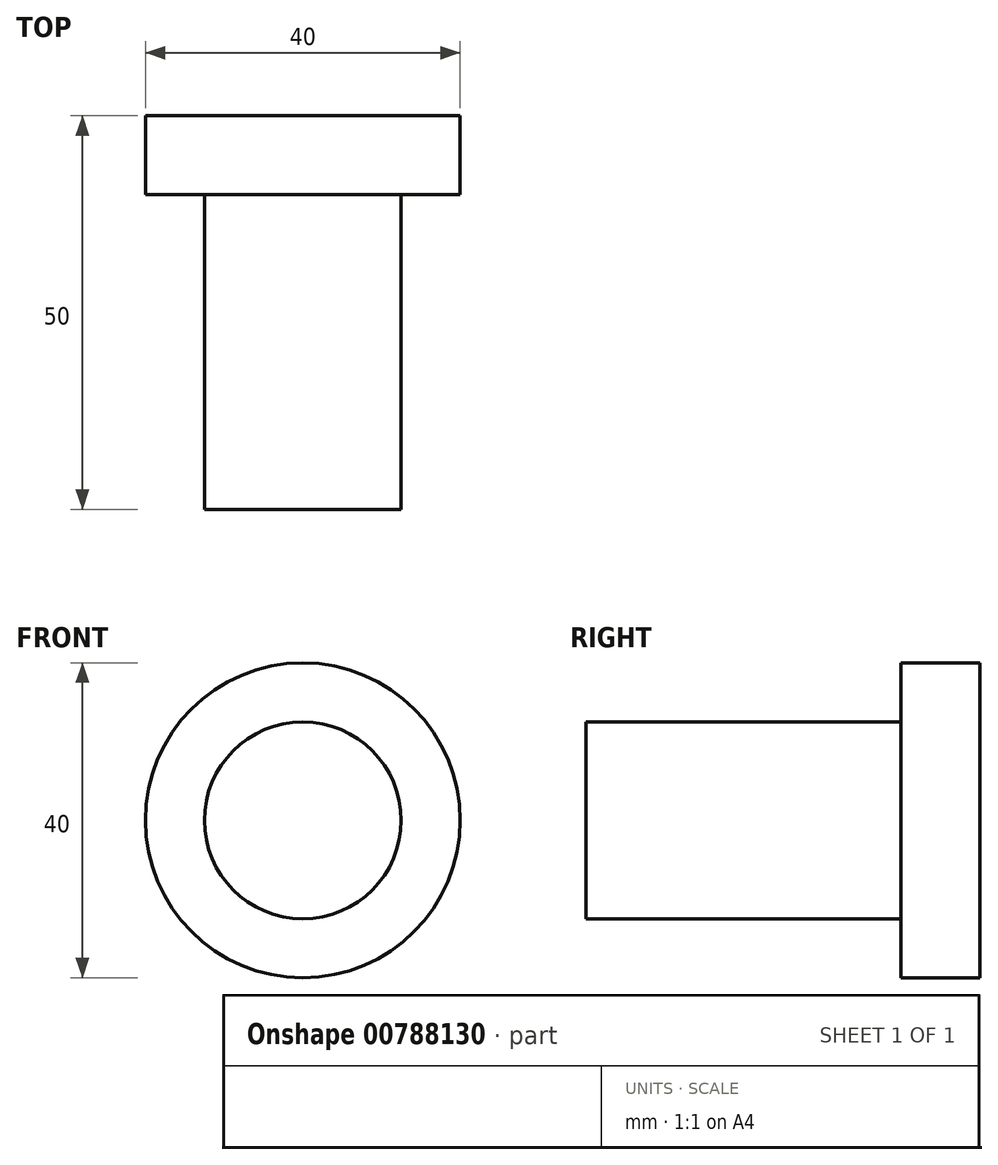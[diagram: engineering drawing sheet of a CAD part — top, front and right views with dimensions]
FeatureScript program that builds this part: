
annotation { "Feature Type Name" : "Feature", "Feature Type Description" : "" }
export const myFeature = defineFeature(function(context is Context, id is Id, definition is map)
    precondition{}
    {
        {
            var Q0;
            Q0=qCreatedBy(makeId("Top.planeOp"),FACE);
            var sketch = newSketch(context, id + "F0", { "sketchPlane" : qUnion([Q0])});
            skLineSegment(sketch, "E0", {"start": v(0, -40) * mm, "end": v(12.5, -40) * mm});
            skLineSegment(sketch, "E1", {"start": v(12.5, -40) * mm, "end": v(12.5, 0) * mm});
            skLineSegment(sketch, "E2", {"start": v(12.5, 0) * mm, "end": v(20, 0) * mm});
            skLineSegment(sketch, "E3", {"start": v(20, 0) * mm, "end": v(20, 10) * mm});
            skLineSegment(sketch, "E4", {"start": v(20, 10) * mm, "end": v(0, 10) * mm});
            skLineSegment(sketch, "E5", {"start": v(0, 10) * mm, "end": v(0, -40) * mm});
            skLineSegment(sketch, "E6", {"start": v(0, 66.35) * mm, "end": v(0, -66.9) * mm, "construction": true});
            skSolve(sketch);
        }
        {
            var Q0;
            Q0 = qSketchRegion(id + "F0", true);
            var Q1;
            Q1=sQuery(id+"F0.wireOp",EDGE,"E6");
            revolve(context, id + "F1", {"surfaceOperationType" : NewSurfaceOperationType.NEW, "entities" : qUnion([Q0]), "axis" : qUnion([Q1]), "revolveType" : RevolveType.FULL});
        }
    });
